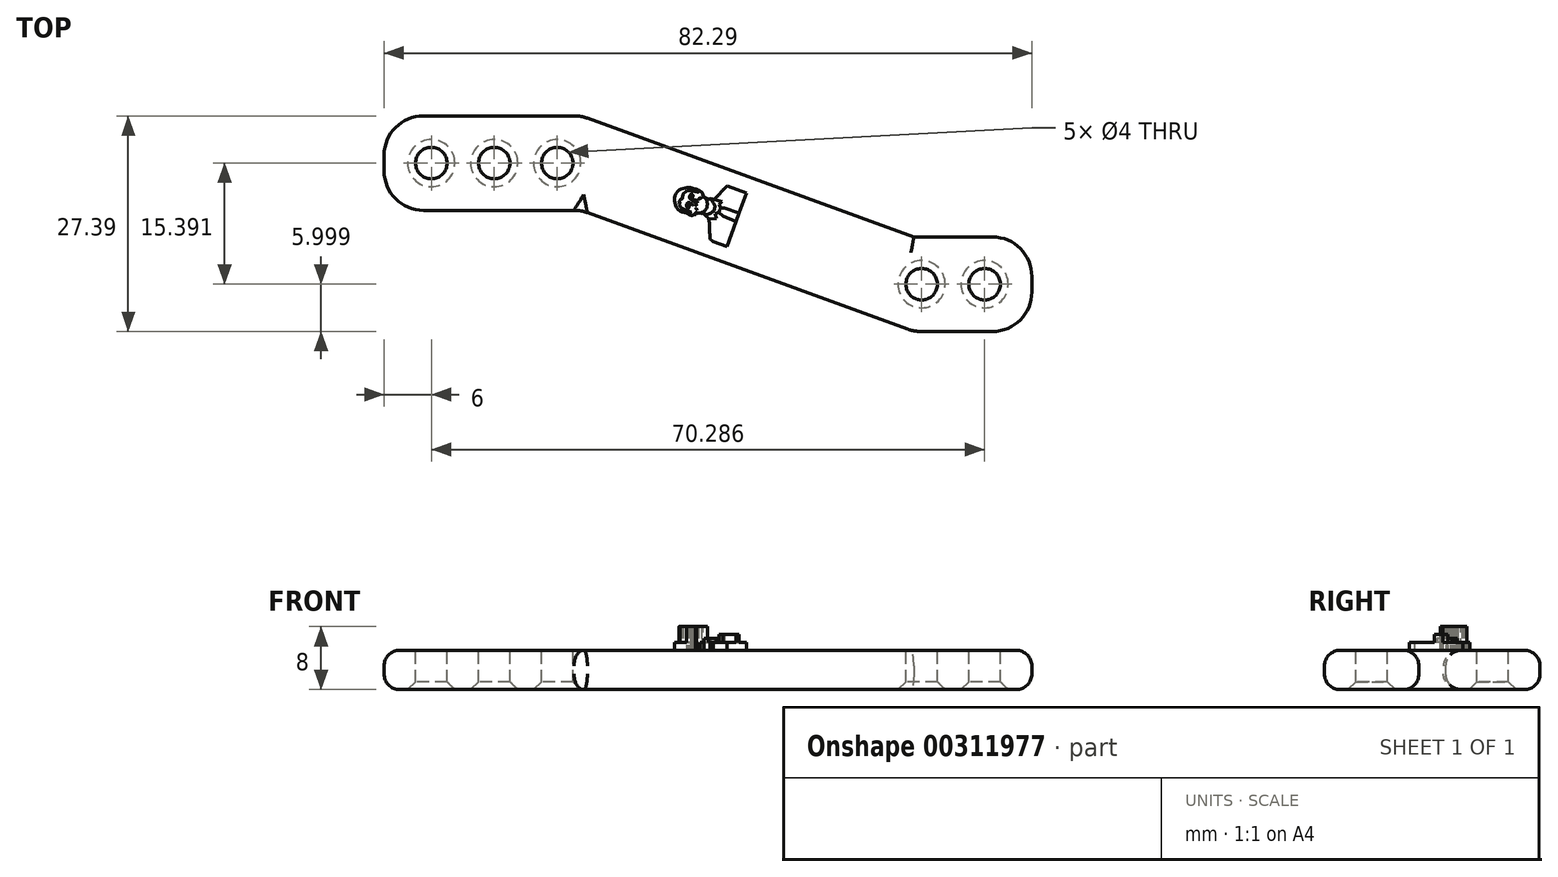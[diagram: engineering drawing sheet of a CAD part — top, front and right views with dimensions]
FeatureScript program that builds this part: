
annotation { "Feature Type Name" : "Feature", "Feature Type Description" : "" }
export const myFeature = defineFeature(function(context is Context, id is Id, definition is map)
    precondition{}
    {
        {
            var Q0;
            Q0=qCreatedBy(makeId("Top.planeOp"),FACE);
            var sketch = newSketch(context, id + "F0", { "sketchPlane" : qUnion([Q0])});
            skLineSegment(sketch, "E0.bottom", {"start": v(0, 12) * mm, "end": v(25, 12) * mm});
            skLineSegment(sketch, "E0.top", {"start": v(0, 0) * mm, "end": v(25, 0) * mm});
            skLineSegment(sketch, "E0.left", {"start": v(0, 12) * mm, "end": v(0, 0) * mm});
            skLineSegment(sketch, "E0.right", {"start": v(25, 12) * mm, "end": v(25, 0) * mm});
            skLineSegment(sketch, "E1.bottom", {"start": v(67.29, -3.4) * mm, "end": v(82.29, -3.4) * mm});
            skLineSegment(sketch, "E1.top", {"start": v(67.29, -15.4) * mm, "end": v(82.29, -15.4) * mm});
            skLineSegment(sketch, "E1.left", {"start": v(67.29, -3.4) * mm, "end": v(67.29, -15.4) * mm});
            skLineSegment(sketch, "E1.right", {"start": v(82.29, -3.4) * mm, "end": v(82.29, -15.4) * mm});
            skLineSegment(sketch, "E2", {"start": v(25, 12) * mm, "end": v(67.29, -3.4) * mm});
            skLineSegment(sketch, "E3", {"start": v(25, 0) * mm, "end": v(67.29, -15.4) * mm});
            skSolve(sketch);
        }
        {
            var Q0;
            Q0=makeQuery(id+"F0.imprint","IMPRINT",FACE,{"disambiguationData":[TD([[makeQuery(id+"F0.imprint","IMPRINT",EDGE,{"derivedFrom":sQuery(id+"F0.wireOp",EDGE,"E0.bottom")}),-1.0]])]});
            var Q1;
            Q1=makeQuery(id+"F0.imprint","IMPRINT",FACE,{"disambiguationData":[TD([[makeQuery(id+"F0.imprint","IMPRINT",EDGE,{"derivedFrom":sQuery(id+"F0.wireOp",EDGE,"E0.right")}),1.0]])]});
            var Q2;
            Q2=makeQuery(id+"F0.imprint","IMPRINT",FACE,{"disambiguationData":[TD([[makeQuery(id+"F0.imprint","IMPRINT",EDGE,{"derivedFrom":sQuery(id+"F0.wireOp",EDGE,"E1.bottom")}),-1.0]])]});
            extrude(context, id + "F1", {"entities" : qUnion([Q0, Q1, Q2]), "depth" : 5 * mm});
        }
        {
            var Q0;
            Q0=makeQuery(id+"F1.opExtrude","CAP_FACE",FACE,{"disambiguationData":[OSD([sQuery(id+"F0.wireOp",EDGE,"E0.bottom"),sQuery(id+"F0.wireOp",EDGE,"E0.top"),sQuery(id+"F0.wireOp",EDGE,"E0.left"),sQuery(id+"F0.wireOp",EDGE,"E1.bottom"),sQuery(id+"F0.wireOp",EDGE,"E1.top"),sQuery(id+"F0.wireOp",EDGE,"E1.right"),sQuery(id+"F0.wireOp",EDGE,"E2"),sQuery(id+"F0.wireOp",EDGE,"E3")])],"isStart":false});
            var sketch = newSketch(context, id + "F2", { "sketchPlane" : qUnion([Q0])});
            skCircle(sketch, "E4", {"center": v(6, 6) * mm, "radius": 2 * mm});
            skCircle(sketch, "E5", {"center": v(76.29, -9.4) * mm, "radius": 2 * mm});
            skCircle(sketch, "E6.1.0.0", {"center": v(14, 6) * mm, "radius": 2 * mm});
            skCircle(sketch, "E6.2.0.0", {"center": v(22, 6) * mm, "radius": 2 * mm});
            skLineSegment(sketch, "E6.direction1", {"start": v(6, 6) * mm, "end": v(14, 6) * mm, "construction": true});
            skCircle(sketch, "E7.1.0.0", {"center": v(68.29, -9.4) * mm, "radius": 2 * mm});
            skLineSegment(sketch, "E7.direction1", {"start": v(76.29, -9.4) * mm, "end": v(68.29, -9.4) * mm, "construction": true});
            skSolve(sketch);
        }
        {
            var Q0;
            Q0 = qSketchRegion(id + "F2", true);
            extrude(context, id + "F3", {"entities" : qUnion([Q0]), "operationType" : NewBodyOperationType.REMOVE, "endBound" : BoundingType.THROUGH_ALL, "oppositeDirection" : true, "depth" : 25 * mm});
        }
        {
            var Q0;
            Q0=makeQuery(id+"F1.opExtrude","CAP_EDGE",EDGE,{"disambiguationData":[OSD([sQuery(id+"F0.wireOp",EDGE,"E0.bottom")])],"isStart":false});
            var Q1;
            Q1=makeQuery(id+"F1.opExtrude","CAP_EDGE",EDGE,{"disambiguationData":[OSD([sQuery(id+"F0.wireOp",EDGE,"E2")])],"isStart":false});
            var Q2;
            Q2=makeQuery(id+"F1.opExtrude","CAP_EDGE",EDGE,{"disambiguationData":[OSD([sQuery(id+"F0.wireOp",EDGE,"E1.bottom")])],"isStart":false});
            var Q3;
            Q3=makeQuery(id+"F1.opExtrude","CAP_EDGE",EDGE,{"disambiguationData":[OSD([sQuery(id+"F0.wireOp",EDGE,"E1.right")])],"isStart":false});
            var Q4;
            Q4=makeQuery(id+"F1.opExtrude","CAP_EDGE",EDGE,{"disambiguationData":[OSD([sQuery(id+"F0.wireOp",EDGE,"E1.top")])],"isStart":false});
            var Q5;
            Q5=makeQuery(id+"F1.opExtrude","CAP_EDGE",EDGE,{"disambiguationData":[OSD([sQuery(id+"F0.wireOp",EDGE,"E3")])],"isStart":false});
            var Q6;
            Q6=makeQuery(id+"F1.opExtrude","CAP_EDGE",EDGE,{"disambiguationData":[OSD([sQuery(id+"F0.wireOp",EDGE,"E0.left")])],"isStart":false});
            var Q7;
            Q7=makeQuery(id+"F1.opExtrude","CAP_EDGE",EDGE,{"disambiguationData":[OSD([sQuery(id+"F0.wireOp",EDGE,"E0.top")])],"isStart":false});
            fillet(context, id + "F4", {"entities" : qUnion([Q0, Q1, Q2, Q3, Q4, Q5, Q6, Q7]), "radius" : 2 * mm, "tangentPropagation" : true, "allowEdgeOverflow" : false});
        }
        {
            var Q0;
            Q0=makeQuery(id+"F1.opExtrude","CAP_EDGE",EDGE,{"disambiguationData":[OSD([sQuery(id+"F0.wireOp",EDGE,"E2")])],"isStart":true});
            var Q1;
            Q1=makeQuery(id+"F1.opExtrude","CAP_EDGE",EDGE,{"disambiguationData":[OSD([sQuery(id+"F0.wireOp",EDGE,"E1.bottom")])],"isStart":true});
            var Q2;
            Q2=makeQuery(id+"F1.opExtrude","CAP_EDGE",EDGE,{"disambiguationData":[OSD([sQuery(id+"F0.wireOp",EDGE,"E1.right")])],"isStart":true});
            var Q3;
            Q3=makeQuery(id+"F1.opExtrude","CAP_EDGE",EDGE,{"disambiguationData":[OSD([sQuery(id+"F0.wireOp",EDGE,"E1.top")])],"isStart":true});
            var Q4;
            Q4=makeQuery(id+"F1.opExtrude","CAP_EDGE",EDGE,{"disambiguationData":[OSD([sQuery(id+"F0.wireOp",EDGE,"E3")])],"isStart":true});
            var Q5;
            Q5=makeQuery(id+"F1.opExtrude","CAP_EDGE",EDGE,{"disambiguationData":[OSD([sQuery(id+"F0.wireOp",EDGE,"E0.top")])],"isStart":true});
            var Q6;
            Q6=makeQuery(id+"F1.opExtrude","CAP_EDGE",EDGE,{"disambiguationData":[OSD([sQuery(id+"F0.wireOp",EDGE,"E0.left")])],"isStart":true});
            var Q7;
            Q7=makeQuery(id+"F1.opExtrude","CAP_EDGE",EDGE,{"disambiguationData":[OSD([sQuery(id+"F0.wireOp",EDGE,"E0.bottom")])],"isStart":true});
            fillet(context, id + "F5", {"entities" : qUnion([Q0, Q1, Q2, Q3, Q4, Q5, Q6, Q7]), "radius" : 2 * mm, "tangentPropagation" : true, "allowEdgeOverflow" : false});
        }
        {
            var Q0;
            Q0=makeQuery(id+"F1.opExtrude","SWEPT_EDGE",EDGE,{"disambiguationData":[OSD([sQuery(id+"F0.wireOp",EDGE,"E1.bottom"),sQuery(id+"F0.wireOp",EDGE,"E1.right")])]});
            var Q1;
            Q1=makeQuery(id+"F1.opExtrude","SWEPT_EDGE",EDGE,{"disambiguationData":[OSD([sQuery(id+"F0.wireOp",EDGE,"E1.top"),sQuery(id+"F0.wireOp",EDGE,"E1.right")])]});
            var Q2;
            Q2=makeQuery(id+"F1.opExtrude","SWEPT_EDGE",EDGE,{"disambiguationData":[OSD([sQuery(id+"F0.wireOp",EDGE,"E1.top"),sQuery(id+"F0.wireOp",EDGE,"E1.left"),sQuery(id+"F0.wireOp",EDGE,"E3")])]});
            var Q3;
            Q3=makeQuery(id+"F1.opExtrude","SWEPT_EDGE",EDGE,{"disambiguationData":[OSD([sQuery(id+"F0.wireOp",EDGE,"E0.top"),sQuery(id+"F0.wireOp",EDGE,"E0.right"),sQuery(id+"F0.wireOp",EDGE,"E3")])]});
            var Q4;
            Q4=makeQuery(id+"F1.opExtrude","SWEPT_EDGE",EDGE,{"disambiguationData":[OSD([sQuery(id+"F0.wireOp",EDGE,"E0.top"),sQuery(id+"F0.wireOp",EDGE,"E0.left")])]});
            var Q5;
            Q5=makeQuery(id+"F1.opExtrude","SWEPT_EDGE",EDGE,{"disambiguationData":[OSD([sQuery(id+"F0.wireOp",EDGE,"E0.bottom"),sQuery(id+"F0.wireOp",EDGE,"E0.left")])]});
            var Q6;
            Q6=makeQuery(id+"F1.opExtrude","SWEPT_EDGE",EDGE,{"disambiguationData":[OSD([sQuery(id+"F0.wireOp",EDGE,"E0.bottom"),sQuery(id+"F0.wireOp",EDGE,"E0.right"),sQuery(id+"F0.wireOp",EDGE,"E2")])]});
            fillet(context, id + "F6", {"entities" : qUnion([Q0, Q1, Q2, Q3, Q4, Q5, Q6]), "radius" : 5 * mm, "tangentPropagation" : true, "allowEdgeOverflow" : false});
        }
        {
            var Q0;
            Q0=makeQuery(id+"F3.boolean.opBoolean","INTERSECT",EDGE,{"derivedFrom":[makeQuery(id+"F1.opExtrude","CAP_FACE",FACE,{"disambiguationData":[OSD([sQuery(id+"F0.wireOp",EDGE,"E0.bottom"),sQuery(id+"F0.wireOp",EDGE,"E0.top"),sQuery(id+"F0.wireOp",EDGE,"E0.left"),sQuery(id+"F0.wireOp",EDGE,"E1.bottom"),sQuery(id+"F0.wireOp",EDGE,"E1.top"),sQuery(id+"F0.wireOp",EDGE,"E1.right"),sQuery(id+"F0.wireOp",EDGE,"E2"),sQuery(id+"F0.wireOp",EDGE,"E3")])],"isStart":true}),makeQuery(id+"F3.opExtrude","SWEPT_FACE",FACE,{"disambiguationData":[OSD([sQuery(id+"F2.wireOp",EDGE,"E5")])]})]});
            var Q1;
            Q1=makeQuery(id+"F3.boolean.opBoolean","INTERSECT",EDGE,{"derivedFrom":[makeQuery(id+"F1.opExtrude","CAP_FACE",FACE,{"disambiguationData":[OSD([sQuery(id+"F0.wireOp",EDGE,"E0.bottom"),sQuery(id+"F0.wireOp",EDGE,"E0.top"),sQuery(id+"F0.wireOp",EDGE,"E0.left"),sQuery(id+"F0.wireOp",EDGE,"E1.bottom"),sQuery(id+"F0.wireOp",EDGE,"E1.top"),sQuery(id+"F0.wireOp",EDGE,"E1.right"),sQuery(id+"F0.wireOp",EDGE,"E2"),sQuery(id+"F0.wireOp",EDGE,"E3")])],"isStart":true}),makeQuery(id+"F3.opExtrude","SWEPT_FACE",FACE,{"disambiguationData":[OSD([sQuery(id+"F2.wireOp",EDGE,"E7.1.0.0")])]})]});
            var Q2;
            Q2=makeQuery(id+"F3.boolean.opBoolean","INTERSECT",EDGE,{"derivedFrom":[makeQuery(id+"F1.opExtrude","CAP_FACE",FACE,{"disambiguationData":[OSD([sQuery(id+"F0.wireOp",EDGE,"E0.bottom"),sQuery(id+"F0.wireOp",EDGE,"E0.top"),sQuery(id+"F0.wireOp",EDGE,"E0.left"),sQuery(id+"F0.wireOp",EDGE,"E1.bottom"),sQuery(id+"F0.wireOp",EDGE,"E1.top"),sQuery(id+"F0.wireOp",EDGE,"E1.right"),sQuery(id+"F0.wireOp",EDGE,"E2"),sQuery(id+"F0.wireOp",EDGE,"E3")])],"isStart":true}),makeQuery(id+"F3.opExtrude","SWEPT_FACE",FACE,{"disambiguationData":[OSD([sQuery(id+"F2.wireOp",EDGE,"E6.2.0.0")])]})]});
            var Q3;
            Q3=makeQuery(id+"F3.boolean.opBoolean","INTERSECT",EDGE,{"derivedFrom":[makeQuery(id+"F1.opExtrude","CAP_FACE",FACE,{"disambiguationData":[OSD([sQuery(id+"F0.wireOp",EDGE,"E0.bottom"),sQuery(id+"F0.wireOp",EDGE,"E0.top"),sQuery(id+"F0.wireOp",EDGE,"E0.left"),sQuery(id+"F0.wireOp",EDGE,"E1.bottom"),sQuery(id+"F0.wireOp",EDGE,"E1.top"),sQuery(id+"F0.wireOp",EDGE,"E1.right"),sQuery(id+"F0.wireOp",EDGE,"E2"),sQuery(id+"F0.wireOp",EDGE,"E3")])],"isStart":true}),makeQuery(id+"F3.opExtrude","SWEPT_FACE",FACE,{"disambiguationData":[OSD([sQuery(id+"F2.wireOp",EDGE,"E4")])]})]});
            var Q4;
            Q4=makeQuery(id+"F3.boolean.opBoolean","COPY",EDGE,{"derivedFrom":makeQuery(id+"F3.opExtrude","CAP_EDGE",EDGE,{"disambiguationData":[OSD([sQuery(id+"F2.wireOp",EDGE,"E4")])],"isStart":true})});
            var Q5;
            Q5=makeQuery(id+"F3.boolean.opBoolean","COPY",EDGE,{"derivedFrom":makeQuery(id+"F3.opExtrude","CAP_EDGE",EDGE,{"disambiguationData":[OSD([sQuery(id+"F2.wireOp",EDGE,"E6.1.0.0")])],"isStart":true})});
            var Q6;
            Q6=makeQuery(id+"F3.boolean.opBoolean","INTERSECT",EDGE,{"derivedFrom":[makeQuery(id+"F1.opExtrude","CAP_FACE",FACE,{"disambiguationData":[OSD([sQuery(id+"F0.wireOp",EDGE,"E0.bottom"),sQuery(id+"F0.wireOp",EDGE,"E0.top"),sQuery(id+"F0.wireOp",EDGE,"E0.left"),sQuery(id+"F0.wireOp",EDGE,"E1.bottom"),sQuery(id+"F0.wireOp",EDGE,"E1.top"),sQuery(id+"F0.wireOp",EDGE,"E1.right"),sQuery(id+"F0.wireOp",EDGE,"E2"),sQuery(id+"F0.wireOp",EDGE,"E3")])],"isStart":true}),makeQuery(id+"F3.opExtrude","SWEPT_FACE",FACE,{"disambiguationData":[OSD([sQuery(id+"F2.wireOp",EDGE,"E6.1.0.0")])]})]});
            var Q7;
            Q7=makeQuery(id+"F3.boolean.opBoolean","COPY",EDGE,{"derivedFrom":makeQuery(id+"F3.opExtrude","CAP_EDGE",EDGE,{"disambiguationData":[OSD([sQuery(id+"F2.wireOp",EDGE,"E6.2.0.0")])],"isStart":true})});
            var Q8;
            Q8=makeQuery(id+"F3.boolean.opBoolean","COPY",EDGE,{"derivedFrom":makeQuery(id+"F3.opExtrude","CAP_EDGE",EDGE,{"disambiguationData":[OSD([sQuery(id+"F2.wireOp",EDGE,"E5")])],"isStart":true})});
            var Q9;
            Q9=makeQuery(id+"F3.boolean.opBoolean","COPY",EDGE,{"derivedFrom":makeQuery(id+"F3.opExtrude","CAP_EDGE",EDGE,{"disambiguationData":[OSD([sQuery(id+"F2.wireOp",EDGE,"E7.1.0.0")])],"isStart":true})});
            chamfer(context, id + "F7", {"entities" : qUnion([Q0, Q1, Q2, Q3, Q4, Q5, Q6, Q7, Q8, Q9]), "width" : 1 * mm, "tangentPropagation" : true});
        }
        {
            var Q0;
            Q0=makeQuery(id+"F1.opExtrude","CAP_FACE",FACE,{"disambiguationData":[OSD([sQuery(id+"F0.wireOp",EDGE,"E0.bottom"),sQuery(id+"F0.wireOp",EDGE,"E0.top"),sQuery(id+"F0.wireOp",EDGE,"E0.left"),sQuery(id+"F0.wireOp",EDGE,"E1.bottom"),sQuery(id+"F0.wireOp",EDGE,"E1.top"),sQuery(id+"F0.wireOp",EDGE,"E1.right"),sQuery(id+"F0.wireOp",EDGE,"E2"),sQuery(id+"F0.wireOp",EDGE,"E3")])],"isStart":false});
            var sketch = newSketch(context, id + "F8", { "sketchPlane" : qUnion([Q0])});
            skFitSpline(sketch, "E8", {"points": [v(38.42, -0.36) * mm, v(37.67, -0.1) * mm, v(37.1, 0.5) * mm, v(36.88, 1.38) * mm, v(37.11, 2.2) * mm, v(37.64, 2.66) * mm, v(38.31, 2.85) * mm, v(38.8, 2.87) * mm, v(39.17, 2.84) * mm, v(39.44, 2.68) * mm, v(39.53, 2.6) * mm, v(39.57, 2.7) * mm, v(40.2, 2.4) * mm, v(40.5, 2.02) * mm, v(40.44, 1.88) * mm, v(40.55, 1.8) * mm, v(40.84, 1.52) * mm, v(41.05, 0.96) * mm, v(40.9, 0.17) * mm, v(40.51, -0.18) * mm, v(39.96, -0.36) * mm, v(39.56, -0.29) * mm, v(39.53, -0.3) * mm, v(39.66, -0.37) * mm, v(39.58, -0.54) * mm, v(39.37, -0.54) * mm, v(39.12, -0.63) * mm, v(38.82, -0.56) * mm, v(38.42, -0.36) * mm]});
            skFitSpline(sketch, "E9", {"points": [v(38.84, 0.8) * mm, v(38.73, 0.39) * mm, v(38.68, 0.31) * mm, v(38.6, 0.6) * mm, v(38.77, 0.97) * mm, v(38.88, 0.95) * mm, v(38.84, 0.8) * mm]});
            skFitSpline(sketch, "E10", {"points": [v(39.04, 1.44) * mm, v(39.1, 1.45) * mm, v(39.23, 1.81) * mm, v(39.27, 1.9) * mm, v(39.09, 1.88) * mm, v(39.04, 1.44) * mm]});
            skFitSpline(sketch, "E11", {"points": [v(39.53, 2.6) * mm, v(39.7, 2.41) * mm, v(39.92, 2.34) * mm, v(39.93, 2.24) * mm, v(39.86, 2.28) * mm, v(38.45, 2.5) * mm, v(38.29, 2.3) * mm, v(38.16, 2.28) * mm, v(38.07, 2.05) * mm, v(37.86, 2.05) * mm, v(37.97, 1.86) * mm, v(37.9, 1.76) * mm, v(37.92, 1.67) * mm, v(37.8, 1.4) * mm, v(37.67, 1.43) * mm, v(37.46, 0.95) * mm, v(37.6, 0.94) * mm, v(37.45, 0.8) * mm, v(37.51, 0.76) * mm, v(37.61, 0.39) * mm, v(37.69, 0.38) * mm, v(38.07, 0.18) * mm, v(39, -0.25) * mm, v(38.99, -0.32) * mm, v(38.92, -0.3) * mm, v(38.65, -0.23) * mm, v(38.42, -0.36) * mm], "startDerivative": vector(3.46, -5.85) * mm, "endDerivative": vector(-5.35, -4.12) * mm});
            skFitSpline(sketch, "E12", {"points": [v(39.65, 0.3) * mm, v(39.76, 0.06) * mm], "startDerivative": vector(-0.09, -0.28) * mm, "endDerivative": vector(0.29, -0.14) * mm});
            skFitSpline(sketch, "E13", {"points": [v(39.61, 0.79) * mm, v(39.57, 0.74) * mm, v(39.56, 0.66) * mm, v(39.6, 0.63) * mm, v(39.62, 0.62) * mm, v(39.65, 0.62) * mm, v(39.66, 0.65) * mm, v(39.66, 0.69) * mm, v(39.65, 0.73) * mm, v(39.61, 0.79) * mm]});
            skFitSpline(sketch, "E14", {"points": [v(39.78, 1.14) * mm, v(39.74, 1.13) * mm, v(39.73, 1.13) * mm, v(39.72, 1.1) * mm, v(39.71, 1.07) * mm, v(39.72, 1.02) * mm, v(39.75, 1) * mm, v(39.78, 1) * mm, v(39.8, 1.05) * mm, v(39.81, 1.1) * mm, v(39.78, 1.14) * mm]});
            skFitSpline(sketch, "E15", {"points": [v(40.24, 1.3) * mm, v(40.13, 0.94) * mm, v(40.05, 0.65) * mm, v(39.99, 0.48) * mm, v(39.96, 0.4) * mm, v(39.93, 0.34) * mm, v(39.9, 0.3) * mm, v(39.88, 0.28) * mm, v(39.9, 0.28) * mm, v(39.94, 0.3) * mm, v(39.97, 0.3) * mm, v(39.97, 0.3) * mm, v(40.03, 0.36) * mm, v(40.05, 0.4) * mm, v(40.06, 0.44) * mm, v(40.08, 0.49) * mm, v(40.1, 0.5) * mm, v(40.13, 0.5) * mm, v(40.15, 0.52) * mm, v(40.16, 0.54) * mm, v(40.18, 0.57) * mm, v(40.21, 0.62) * mm, v(40.25, 0.68) * mm, v(40.27, 0.75) * mm, v(40.3, 0.8) * mm, v(40.3, 0.86) * mm, v(40.31, 0.91) * mm, v(40.31, 0.98) * mm, v(40.3, 1.04) * mm, v(40.3, 1.1) * mm, v(40.3, 1.16) * mm, v(40.3, 1.18) * mm, v(40.3, 1.2) * mm, v(40.3, 1.24) * mm, v(40.28, 1.27) * mm, v(40.24, 1.3) * mm]});
            skFitSpline(sketch, "E16", {"points": [v(40.33, 1.53) * mm, v(40.3, 1.55) * mm, v(40.21, 1.57) * mm, v(40.17, 1.57) * mm, v(40.1, 1.55) * mm, v(40.03, 1.52) * mm, v(40, 1.51) * mm, v(39.94, 1.46) * mm, v(39.91, 1.4) * mm, v(39.98, 1.4) * mm, v(40.03, 1.46) * mm, v(40.08, 1.5) * mm, v(40.2, 1.53) * mm, v(40.24, 1.53) * mm, v(40.29, 1.52) * mm, v(40.33, 1.53) * mm]});
            skFitSpline(sketch, "E17", {"points": [v(39.65, 0.3) * mm, v(39.64, 0.23) * mm, v(39.65, 0.18) * mm], "startDerivative": vector(-0.03, -0.13) * mm, "endDerivative": vector(0.03, -0.11) * mm});
            skFitSpline(sketch, "E18", {"points": [v(39.65, 0.3) * mm, v(39.66, 0.24) * mm, v(39.66, 0.21) * mm, v(39.68, 0.18) * mm, v(39.69, 0.16) * mm, v(39.7, 0.14) * mm, v(39.71, 0.12) * mm, v(39.73, 0.1) * mm, v(39.74, 0.07) * mm, v(39.76, 0.06) * mm], "startDerivative": vector(0.1, -0.46) * mm, "endDerivative": vector(0.12, -0.2) * mm});
            skFitSpline(sketch, "E19", {"points": [v(38.7, 0.99) * mm, v(38.69, 0.98) * mm, v(38.66, 0.96) * mm, v(38.62, 0.93) * mm, v(38.6, 0.9) * mm, v(38.57, 0.83) * mm, v(38.54, 0.76) * mm, v(38.53, 0.7) * mm, v(38.5, 0.63) * mm, v(38.5, 0.57) * mm, v(38.51, 0.53) * mm, v(38.53, 0.44) * mm, v(38.54, 0.4) * mm, v(38.56, 0.33) * mm, v(38.57, 0.3) * mm, v(38.54, 0.3) * mm, v(38.5, 0.35) * mm, v(38.49, 0.38) * mm, v(38.46, 0.45) * mm, v(38.44, 0.5) * mm, v(38.43, 0.56) * mm, v(38.42, 0.64) * mm, v(38.42, 0.7) * mm, v(38.43, 0.76) * mm, v(38.44, 0.78) * mm, v(38.47, 0.85) * mm, v(38.5, 0.9) * mm, v(38.56, 0.97) * mm, v(38.6, 1) * mm, v(38.64, 1) * mm, v(38.7, 0.99) * mm]});
            skFitSpline(sketch, "E20", {"points": [v(39.21, 2.11) * mm, v(39.15, 2.1) * mm, v(39.07, 2.08) * mm, v(39, 2.05) * mm, v(38.94, 2) * mm, v(38.9, 1.98) * mm, v(38.86, 1.91) * mm, v(38.8, 1.84) * mm, v(38.8, 1.76) * mm, v(38.8, 1.68) * mm, v(38.8, 1.6) * mm, v(38.8, 1.55) * mm, v(38.86, 1.48) * mm, v(38.9, 1.51) * mm, v(38.89, 1.56) * mm, v(38.88, 1.65) * mm, v(38.88, 1.72) * mm, v(38.9, 1.8) * mm, v(38.93, 1.84) * mm, v(38.95, 1.89) * mm, v(39.02, 1.97) * mm, v(39.1, 2.02) * mm, v(39.15, 2.06) * mm, v(39.21, 2.11) * mm]});
            skFitSpline(sketch, "E21", {"points": [v(39.1, 1.23) * mm, v(39.15, 1.2) * mm, v(39.21, 1.17) * mm, v(39.27, 1.16) * mm, v(39.36, 1.14) * mm, v(39.43, 1.12) * mm, v(39.52, 1.1) * mm, v(39.6, 1.14) * mm, v(39.68, 1.2) * mm, v(39.67, 1.26) * mm, v(39.54, 1.3) * mm, v(39.45, 1.33) * mm, v(39.38, 1.33) * mm, v(39.29, 1.33) * mm, v(39.2, 1.3) * mm, v(39.17, 1.3) * mm, v(39.1, 1.23) * mm]});
            skFitSpline(sketch, "E22", {"points": [v(39.07, 0.83) * mm, v(39.11, 0.78) * mm, v(39.15, 0.7) * mm, v(39.23, 0.67) * mm, v(39.23, 0.72) * mm, v(39.18, 0.8) * mm, v(39.07, 0.83) * mm]});
            skFitSpline(sketch, "E23", {"points": [v(38.82, 0.72) * mm, v(38.73, 0.72) * mm, v(38.66, 0.7) * mm, v(38.6, 0.6) * mm], "startDerivative": vector(-0.3, 0) * mm, "endDerivative": vector(-0.16, -0.32) * mm});
            skFitSpline(sketch, "E24", {"points": [v(39.25, 1.85) * mm, v(39.18, 1.84) * mm, v(39.13, 1.81) * mm, v(39.1, 1.77) * mm, v(39.08, 1.73) * mm, v(39.07, 1.65) * mm, v(39.08, 1.58) * mm, v(39.14, 1.53) * mm, v(39.13, 1.5) * mm], "startDerivative": vector(-0.53, -0.01) * mm, "endDerivative": vector(-0.2, -0.23) * mm});
            skFitSpline(sketch, "E25", {"points": [v(40.13, -0.34) * mm, v(40.31, -0.38) * mm, v(40.47, -0.38) * mm, v(40.63, -0.43) * mm, v(40.8, -0.5) * mm, v(40.97, -0.53) * mm, v(41.15, -0.5) * mm, v(41.27, -0.46) * mm, v(41.37, -0.41) * mm, v(41.5, -0.35) * mm, v(41.58, -0.29) * mm, v(41.76, -0.15) * mm, v(41.9, 0) * mm, v(41.98, 0.18) * mm, v(42, 0.3) * mm, v(42.06, 0.44) * mm, v(42.02, 0.6) * mm, v(41.96, 0.73) * mm, v(41.87, 0.86) * mm, v(41.8, 0.98) * mm, v(41.74, 1.14) * mm, v(41.68, 1.2) * mm, v(41.59, 1.31) * mm, v(41.46, 1.4) * mm, v(41.32, 1.4) * mm, v(40.73, 1.65) * mm], "startDerivative": vector(4.27, -1.1) * mm, "endDerivative": vector(-8.79, 4.43) * mm});
            skFitSpline(sketch, "E26", {"points": [v(40.63, -0.43) * mm, v(40.84, -0.7) * mm, v(40.96, -0.78) * mm, v(41.08, -0.86) * mm, v(41.17, -0.94) * mm, v(41.23, -1.1) * mm, v(41.28, -1.28) * mm, v(41.3, -1.47) * mm, v(41.32, -1.72) * mm, v(41.32, -1.95) * mm, v(41.33, -2.23) * mm, v(41.35, -2.5) * mm, v(41.37, -2.71) * mm, v(41.37, -2.87) * mm, v(41.38, -3.07) * mm, v(41.38, -3.24) * mm, v(41.4, -3.49) * mm, v(41.44, -3.63) * mm, v(41.8, -3.99) * mm], "startDerivative": vector(3.05, -4.52) * mm, "endDerivative": vector(5.41, -4.64) * mm});
            skLineSegment(sketch, "E27", {"start": v(41.32, 1.4) * mm, "end": v(41.46, 1.5) * mm});
            skLineSegment(sketch, "E28", {"start": v(41.46, 1.5) * mm, "end": v(42.94, 1.12) * mm});
            skLineSegment(sketch, "E29", {"start": v(42.94, 1.12) * mm, "end": v(42.13, 0.41) * mm});
            skLineSegment(sketch, "E30", {"start": v(42.13, 0.41) * mm, "end": v(41.97, 0) * mm});
            skLineSegment(sketch, "E31", {"start": v(41.97, 0) * mm, "end": v(42.23, -1.07) * mm});
            skLineSegment(sketch, "E32", {"start": v(42.23, -1.07) * mm, "end": v(41.23, -1.1) * mm});
            skLineSegment(sketch, "E33", {"start": v(42.53, 0.77) * mm, "end": v(42.82, 0.3) * mm});
            skLineSegment(sketch, "E34", {"start": v(42.82, 0.3) * mm, "end": v(42.73, 0.22) * mm});
            skLineSegment(sketch, "E35", {"start": v(42.73, 0.22) * mm, "end": v(42.6, 0.05) * mm});
            skLineSegment(sketch, "E36", {"start": v(42.6, 0.05) * mm, "end": v(42.57, -0.25) * mm});
            skLineSegment(sketch, "E37", {"start": v(42.57, -0.25) * mm, "end": v(42.06, -0.38) * mm});
            skLineSegment(sketch, "E38", {"start": v(42.57, -0.25) * mm, "end": v(43.06, -0.75) * mm});
            skLineSegment(sketch, "E39", {"start": v(43.06, -0.75) * mm, "end": v(44.7, -1.44) * mm});
            skLineSegment(sketch, "E40", {"start": v(44.7, -1.44) * mm, "end": v(46.04, 2.21) * mm});
            skLineSegment(sketch, "E41", {"start": v(46.04, 2.21) * mm, "end": v(44.2, 2.91) * mm});
            skLineSegment(sketch, "E42", {"start": v(44.2, 2.91) * mm, "end": v(43.78, 2.82) * mm});
            skFitSpline(sketch, "E43", {"points": [v(39.9, 0.28) * mm, v(40.05, 0.28) * mm, v(40.22, 0.36) * mm, v(40.43, 0.64) * mm, v(40.45, 1.03) * mm, v(40.3, 1.24) * mm], "startDerivative": vector(0.98, -0.08) * mm, "endDerivative": vector(-0.93, 0.9) * mm});
            skFitSpline(sketch, "E44", {"points": [v(41.9, 1.38) * mm, v(42.15, 1.57) * mm, v(42.26, 1.7) * mm, v(42.42, 1.86) * mm, v(42.57, 2.02) * mm, v(42.68, 2.15) * mm, v(42.75, 2.26) * mm, v(42.9, 2.42) * mm, v(43.03, 2.56) * mm, v(43.21, 2.74) * mm, v(43.34, 2.87) * mm, v(43.61, 3.1) * mm], "startDerivative": vector(2.64, 1.71) * mm, "endDerivative": vector(2.7, 2.04) * mm});
            skLineSegment(sketch, "E45", {"start": v(41.8, -3.99) * mm, "end": v(43.55, -4.62) * mm});
            skLineSegment(sketch, "E46", {"start": v(43.55, -4.62) * mm, "end": v(46.04, 2.21) * mm});
            skLineSegment(sketch, "E47", {"start": v(46.04, 2.21) * mm, "end": v(43.61, 3.1) * mm});
            skLineSegment(sketch, "E48", {"start": v(45.1, -0.35) * mm, "end": v(43.27, 0.31) * mm});
            skLineSegment(sketch, "E49", {"start": v(43.27, 0.31) * mm, "end": v(42.82, 0.3) * mm});
            skSolve(sketch);
        }
        {
            var Q0;
            {var subQ13=sQuery(id+"F8.wireOp",EDGE,"E11");Q0=makeQuery(id+"F8.imprint","IMPRINT",FACE,{"disambiguationData":[TD([[makeQuery(id+"F8.imprint","IMPRINT",EDGE,{"derivedFrom":subQ13}),1.0]])]});}
            extrude(context, id + "F9", {"entities" : qUnion([Q0]), "operationType" : NewBodyOperationType.ADD, "depth" : 3 * mm});
        }
        {
            var Q0;
            {var subQ0=sQuery(id+"F8.wireOp",EDGE,"E11");Q0=makeQuery(id+"F8.imprint","IMPRINT",FACE,{"disambiguationData":[TD([[makeQuery(id+"F8.imprint","IMPRINT",EDGE,{"derivedFrom":subQ0}),-1.0]])]});}
            extrude(context, id + "F10", {"entities" : qUnion([Q0]), "operationType" : NewBodyOperationType.ADD, "depth" : 1 * mm});
        }
        {
            var Q0;
            {var subQ0=sQuery(id+"F8.wireOp",EDGE,"E25");var subQ1=sQuery(id+"F8.wireOp",EDGE,"E8");var subQ2=makeQuery(id+"F8.imprint","INTERSECT",VERTEX,{"disambiguationData":[OD(0.0)],"derivedFrom":[subQ1,subQ0]});Q0=makeQuery(id+"F8.imprint","IMPRINT",FACE,{"disambiguationData":[TD([[makeQuery(id+"F8.imprint","IMPRINT",EDGE,{"disambiguationData":[TD([[subQ2,1.0]])],"derivedFrom":subQ1}),1.0]])]});}
            extrude(context, id + "F11", {"entities" : qUnion([Q0]), "operationType" : NewBodyOperationType.ADD, "depth" : 1 * mm});
        }
        {
            var Q0;
            {var subQ4=sQuery(id+"F8.wireOp",EDGE,"E33");Q0=makeQuery(id+"F8.imprint","IMPRINT",FACE,{"disambiguationData":[TD([[makeQuery(id+"F8.imprint","IMPRINT",EDGE,{"derivedFrom":subQ4}),1.0]])]});}
            var Q1;
            {var subQ9=sQuery(id+"F8.wireOp",EDGE,"E26");Q1=makeQuery(id+"F8.imprint","IMPRINT",FACE,{"disambiguationData":[TD([[makeQuery(id+"F8.imprint","IMPRINT",EDGE,{"derivedFrom":subQ9}),1.0]])]});}
            extrude(context, id + "F12", {"entities" : qUnion([Q0, Q1]), "operationType" : NewBodyOperationType.ADD, "depth" : 1 * mm});
        }
        {
            var Q0;
            Q0=makeQuery(id+"F8.imprint","IMPRINT",FACE,{"disambiguationData":[TD([[makeQuery(id+"F8.imprint","IMPRINT",EDGE,{"derivedFrom":sQuery(id+"F8.wireOp",EDGE,"E34")}),1.0]])]});
            extrude(context, id + "F13", {"entities" : qUnion([Q0]), "operationType" : NewBodyOperationType.ADD, "depth" : 2 * mm});
        }
        {
            var Q0;
            {var subQ1=sQuery(id+"F8.wireOp",EDGE,"E30");Q0=makeQuery(id+"F8.imprint","IMPRINT",FACE,{"disambiguationData":[TD([[makeQuery(id+"F8.imprint","IMPRINT",EDGE,{"derivedFrom":subQ1}),1.0]])]});}
            extrude(context, id + "F14", {"entities" : qUnion([Q0]), "operationType" : NewBodyOperationType.ADD, "depth" : 1.5 * mm});
        }
        {
            var Q0;
            {var subQ12=sQuery(id+"F8.wireOp",EDGE,"E27");Q0=makeQuery(id+"F8.imprint","IMPRINT",FACE,{"disambiguationData":[TD([[makeQuery(id+"F8.imprint","IMPRINT",EDGE,{"derivedFrom":subQ12}),-1.0]])]});}
            extrude(context, id + "F15", {"entities" : qUnion([Q0]), "operationType" : NewBodyOperationType.ADD, "depth" : 1.5 * mm});
        }
    });
